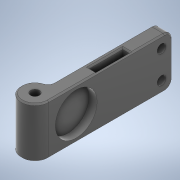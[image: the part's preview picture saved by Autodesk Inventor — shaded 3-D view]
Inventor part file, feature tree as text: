
AUTODESK INVENTOR PART (.ipt)
format: ipt  version: 2020 (Build 240168000, 168)  size: 391,168 bytes
history: native  units: mm
features: extrude x4, sketch x4, fillet x2, chamfer x2
ambient origin geometry x8: Origin, YZ Plane, XZ Plane, XY Plane, X Axis, Y Axis, Z Axis, Center Point
bodies: Volumenkörper1 (feature_tree)
feature tree (12):
  extrude  "Extrusion1"  Depth=2.0mm
  fillet  "Rundung1"  Radius=2.0mm
  chamfer  "Fase1"  Distance=18.2mm
  extrude  "Extrusion2"  Depth=3.0mm
  extrude  "Extrusion3"  Depth=3.2mm
  extrude  "Extrusion5"  Depth=2.0mm
  fillet  "Rundung2"  Radius=19.0mm
  chamfer  "Fase2"  Distance=15.0mm
  sketch  "Skizze1"  dims[d0=3.2mm d2=3.4mm d3=2.0mm]
  sketch  "Skizze2"  dims[d4=45.0mm d5=18.2mm d6=0.0mm]
  sketch  "Skizze3"  dims[d7=0.5mm d8=2.0mm d9=45.0deg d10=3.0mm]
  sketch  "Skizze7"  dims[d11=10.0mm d12=3.2mm d13=4.0mm d14=19.0mm d15=0.0mm d16=15.0mm d17=15.2mm d18=3.0mm d19=0.0mm d23=29.0mm d24=12.2mm d27=5.0mm d28=12.2mm d29=2.8mm d30=0.4mm d31=15.2mm d32=0.0mm d33=17.9mm d34=6.1mm d35=0.5mm d36=2.0mm d37=45.0deg]
